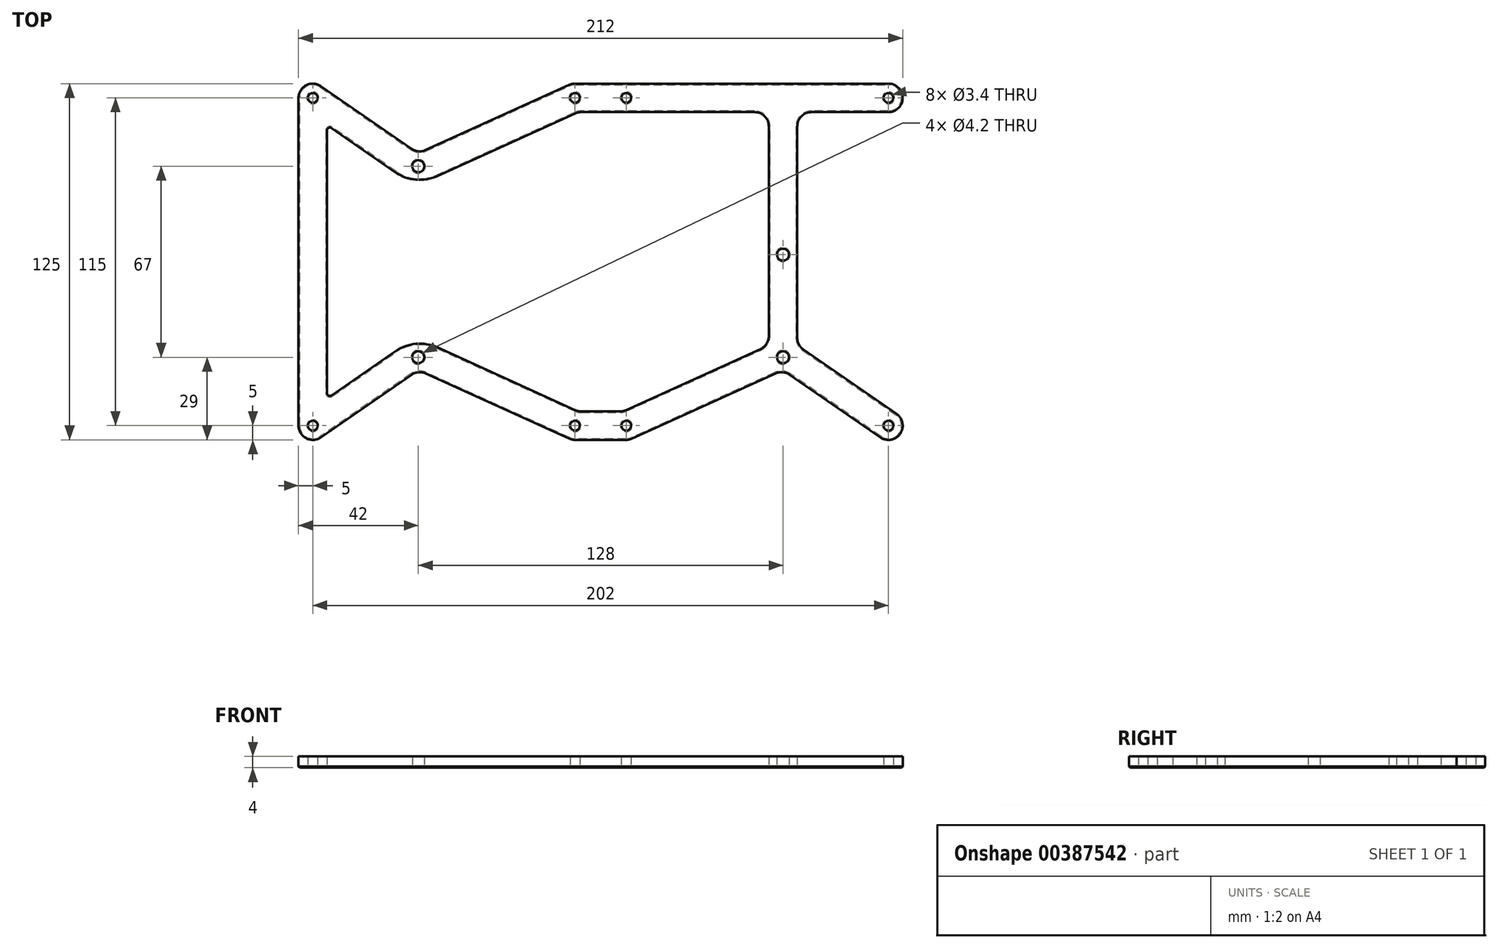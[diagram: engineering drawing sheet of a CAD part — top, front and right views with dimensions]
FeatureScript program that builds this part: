
annotation { "Feature Type Name" : "Feature", "Feature Type Description" : "" }
export const myFeature = defineFeature(function(context is Context, id is Id, definition is map)
    precondition{}
    {
        {
            var Q0;
            Q0=qCreatedBy(makeId("Top.planeOp"),FACE);
            var sketch = newSketch(context, id + "F0", { "sketchPlane" : qUnion([Q0])});
            skLineSegment(sketch, "E0", {"start": v(-64, 33.5) * mm, "end": v(-64, -33.5) * mm, "construction": true});
            skLineSegment(sketch, "E1", {"start": v(-64, -33.5) * mm, "end": v(64, -33.5) * mm, "construction": true});
            skLineSegment(sketch, "E2", {"start": v(64, -33.5) * mm, "end": v(64, 2.5) * mm, "construction": true});
            skLineSegment(sketch, "E3", {"start": v(0, 0) * mm, "end": v(0, -33.5) * mm, "construction": true});
            skCircle(sketch, "E4", {"center": v(-64, 33.5) * mm, "radius": 2.1 * mm});
            skCircle(sketch, "E5", {"center": v(-64, -33.5) * mm, "radius": 2.1 * mm});
            skCircle(sketch, "E6", {"center": v(64, -33.5) * mm, "radius": 2.1 * mm});
            skCircle(sketch, "E7", {"center": v(64, 2.5) * mm, "radius": 2.1 * mm});
            skSolve(sketch);
        }
        {
            var Q0;
            Q0=qCreatedBy(makeId("Top.planeOp"),FACE);
            var sketch = newSketch(context, id + "F1", { "sketchPlane" : qUnion([Q0])});
            skLineSegment(sketch, "E8.bottom", {"start": v(101, 57.5) * mm, "end": v(9, 57.5) * mm, "construction": true});
            skLineSegment(sketch, "E8.top", {"start": v(101, -57.5) * mm, "end": v(9, -57.5) * mm, "construction": true});
            skLineSegment(sketch, "E8.left", {"start": v(101, 57.5) * mm, "end": v(101, -57.5) * mm, "construction": true});
            skLineSegment(sketch, "E8.right", {"start": v(9, 57.5) * mm, "end": v(9, -57.5) * mm, "construction": true});
            skPoint(sketch, "E8.middle", {"position": v(55, 0) * mm});
            skCircle(sketch, "E9", {"center": v(9, 57.5) * mm, "radius": 2.1 * mm});
            skCircle(sketch, "E10", {"center": v(101, 57.5) * mm, "radius": 2.1 * mm});
            skCircle(sketch, "E11", {"center": v(101, -57.5) * mm, "radius": 2.1 * mm});
            skCircle(sketch, "E12", {"center": v(9, -57.5) * mm, "radius": 2.1 * mm});
            skLineSegment(sketch, "E13.0", {"start": v(5, 61.5) * mm, "end": v(5, -61.5) * mm, "construction": true});
            skLineSegment(sketch, "E13.1", {"start": v(105, 61.5) * mm, "end": v(5, 61.5) * mm, "construction": true});
            skLineSegment(sketch, "E13.2", {"start": v(105, 61.5) * mm, "end": v(105, -61.5) * mm, "construction": true});
            skLineSegment(sketch, "E13.3", {"start": v(105, -61.5) * mm, "end": v(5, -61.5) * mm, "construction": true});
            skLineSegment(sketch, "E14", {"start": v(0, 100) * mm, "end": v(0, -100) * mm, "construction": true});
            skCircle(sketch, "E15.MirrorC", {"center": v(-101, 57.5) * mm, "radius": 2.1 * mm});
            skCircle(sketch, "E16.MirrorC", {"center": v(-101, -57.5) * mm, "radius": 2.1 * mm});
            skCircle(sketch, "E17.MirrorC", {"center": v(-9, -57.5) * mm, "radius": 2.1 * mm});
            skCircle(sketch, "E18.MirrorC", {"center": v(-9, 57.5) * mm, "radius": 2.1 * mm});
            skLineSegment(sketch, "E19.MirrorCS", {"start": v(-5, 61.5) * mm, "end": v(-5, -61.5) * mm, "construction": true});
            skLineSegment(sketch, "E20.MirrorCS", {"start": v(-105, 61.5) * mm, "end": v(-5, 61.5) * mm, "construction": true});
            skLineSegment(sketch, "E21.MirrorCS", {"start": v(-105, 61.5) * mm, "end": v(-105, -61.5) * mm, "construction": true});
            skLineSegment(sketch, "E22.MirrorCS", {"start": v(-105, -61.5) * mm, "end": v(-5, -61.5) * mm, "construction": true});
            skPoint(sketch, "E23.MirrorP", {"position": v(-55, 0) * mm});
            skLineSegment(sketch, "E24.MirrorCS", {"start": v(-101, 57.5) * mm, "end": v(-9, 57.5) * mm, "construction": true});
            skLineSegment(sketch, "E25.MirrorCS", {"start": v(-101, -57.5) * mm, "end": v(-9, -57.5) * mm, "construction": true});
            skLineSegment(sketch, "E26.MirrorCS", {"start": v(-9, 57.5) * mm, "end": v(-9, -57.5) * mm, "construction": true});
            skLineSegment(sketch, "E27.MirrorCS", {"start": v(-101, 57.5) * mm, "end": v(-101, -57.5) * mm, "construction": true});
            skCircle(sketch, "E28", {"center": v(-101, 57.5) * mm, "radius": 1.7 * mm});
            skCircle(sketch, "E29", {"center": v(-9, 57.5) * mm, "radius": 1.7 * mm});
            skCircle(sketch, "E30", {"center": v(9, 57.5) * mm, "radius": 1.7 * mm});
            skCircle(sketch, "E31", {"center": v(101, 57.5) * mm, "radius": 1.7 * mm});
            skCircle(sketch, "E32", {"center": v(101, -57.5) * mm, "radius": 1.7 * mm});
            skCircle(sketch, "E33", {"center": v(-9, -57.5) * mm, "radius": 1.7 * mm});
            skCircle(sketch, "E34", {"center": v(9, -57.5) * mm, "radius": 1.7 * mm});
            skCircle(sketch, "E35", {"center": v(-101, -57.5) * mm, "radius": 1.7 * mm});
            skSolve(sketch);
        }
        {
            var Q0;
            Q0=qCreatedBy(makeId("Top.planeOp"),FACE);
            var sketch = newSketch(context, id + "F2", { "sketchPlane" : qUnion([Q0])});
            skLineSegment(sketch, "E36", {"start": v(-98.16, -61.61) * mm, "end": v(-66.33, -39.61) * mm});
            skLineSegment(sketch, "E37", {"start": v(-61.42, -39.17) * mm, "end": v(-11.07, -62.05) * mm});
            skLineSegment(sketch, "E38", {"start": v(-9, -62.5) * mm, "end": v(9, -62.5) * mm});
            skLineSegment(sketch, "E39", {"start": v(11.07, -62.05) * mm, "end": v(61.42, -39.17) * mm});
            skLineSegment(sketch, "E40", {"start": v(66.33, -39.61) * mm, "end": v(98.16, -61.61) * mm});
            skLineSegment(sketch, "E41", {"start": v(103.84, -53.39) * mm, "end": v(71.16, -30.8) * mm});
            skLineSegment(sketch, "E42", {"start": v(69, -26.68) * mm, "end": v(69, 47.5) * mm});
            skLineSegment(sketch, "E43", {"start": v(101, 52.5) * mm, "end": v(74, 52.5) * mm});
            skLineSegment(sketch, "E44", {"start": v(101, 62.5) * mm, "end": v(-9, 62.5) * mm});
            skLineSegment(sketch, "E45", {"start": v(-11.07, 62.05) * mm, "end": v(-61.42, 39.17) * mm});
            skLineSegment(sketch, "E46", {"start": v(-66.33, 39.61) * mm, "end": v(-98.16, 61.61) * mm});
            skLineSegment(sketch, "E47", {"start": v(-106, 57.5) * mm, "end": v(-106, -57.5) * mm});
            skArc(sketch, "E48.filletArc", {"start": v(98.16, -61.61) * mm, "mid": v(105.11, -60.34) * mm, "end": v(103.84, -53.39) * mm});
            skArc(sketch, "E49.filletArc", {"start": v(101, 52.5) * mm, "mid": v(106, 57.5) * mm, "end": v(101, 62.5) * mm});
            skPoint(sketch, "E50.visualSharp", {"position": v(69, 52.5) * mm});
            skArc(sketch, "E50.filletArc", {"start": v(74, 52.5) * mm, "mid": v(70.46, 51.04) * mm, "end": v(69, 47.5) * mm});
            skPoint(sketch, "E51.visualSharp", {"position": v(69, -29.3) * mm});
            skArc(sketch, "E51.filletArc", {"start": v(69, -26.68) * mm, "mid": v(69.57, -29) * mm, "end": v(71.16, -30.8) * mm});
            skPoint(sketch, "E52.visualSharp", {"position": v(10.08, -62.5) * mm});
            skArc(sketch, "E52.filletArc", {"start": v(9, -62.5) * mm, "mid": v(10.06, -62.39) * mm, "end": v(11.07, -62.05) * mm});
            skPoint(sketch, "E53.visualSharp", {"position": v(-10.08, -62.5) * mm});
            skArc(sketch, "E53.filletArc", {"start": v(-11.07, -62.05) * mm, "mid": v(-10.06, -62.39) * mm, "end": v(-9, -62.5) * mm});
            skPoint(sketch, "E54.visualSharp", {"position": v(-64, -38) * mm});
            skArc(sketch, "E54.filletArc", {"start": v(-61.42, -39.17) * mm, "mid": v(-63.93, -38.74) * mm, "end": v(-66.33, -39.61) * mm});
            skPoint(sketch, "E55.visualSharp", {"position": v(64, -38) * mm});
            skArc(sketch, "E55.filletArc", {"start": v(66.33, -39.61) * mm, "mid": v(63.93, -38.74) * mm, "end": v(61.42, -39.17) * mm});
            skPoint(sketch, "E56.visualSharp", {"position": v(-106, -67.04) * mm});
            skArc(sketch, "E56.filletArc", {"start": v(-106, -57.5) * mm, "mid": v(-103.32, -61.93) * mm, "end": v(-98.16, -61.61) * mm});
            skPoint(sketch, "E57.visualSharp", {"position": v(-106, 67.04) * mm});
            skArc(sketch, "E57.filletArc", {"start": v(-98.16, 61.61) * mm, "mid": v(-103.32, 61.93) * mm, "end": v(-106, 57.5) * mm});
            skPoint(sketch, "E58.visualSharp", {"position": v(-64, 38) * mm});
            skArc(sketch, "E58.filletArc", {"start": v(-66.33, 39.61) * mm, "mid": v(-63.93, 38.74) * mm, "end": v(-61.42, 39.17) * mm});
            skPoint(sketch, "E59.visualSharp", {"position": v(-10.08, 62.5) * mm});
            skArc(sketch, "E59.filletArc", {"start": v(-9, 62.5) * mm, "mid": v(-10.06, 62.39) * mm, "end": v(-11.07, 62.05) * mm});
            skLineSegment(sketch, "E60", {"start": v(-64, -38) * mm, "end": v(-64, -33.5) * mm, "construction": true});
            skLineSegment(sketch, "E61", {"start": v(64, -38) * mm, "end": v(64, -33.5) * mm, "construction": true});
            skLineSegment(sketch, "E62", {"start": v(-64, 38) * mm, "end": v(-64, 33.5) * mm, "construction": true});
            skArc(sketch, "E63.0", {"start": v(-57.28, -30.07) * mm, "mid": v(-64.82, -28.78) * mm, "end": v(-72.02, -31.39) * mm});
            skLineSegment(sketch, "E63.1", {"start": v(-94.43, -46.88) * mm, "end": v(-72.02, -31.39) * mm});
            skLineSegment(sketch, "E63.2", {"start": v(-96, 46.06) * mm, "end": v(-96, -46.06) * mm});
            skLineSegment(sketch, "E63.5", {"start": v(8.9, -52.05) * mm, "end": v(56.07, -30.62) * mm});
            skLineSegment(sketch, "E63.6", {"start": v(-6.83, -52.5) * mm, "end": v(6.83, -52.5) * mm});
            skLineSegment(sketch, "E63.7", {"start": v(59, -26.07) * mm, "end": v(59, 47.5) * mm});
            skLineSegment(sketch, "E63.9", {"start": v(54, 52.5) * mm, "end": v(-6.83, 52.5) * mm});
            skLineSegment(sketch, "E63.10", {"start": v(-57.28, -30.07) * mm, "end": v(-8.9, -52.05) * mm});
            skLineSegment(sketch, "E63.11", {"start": v(-8.9, 52.05) * mm, "end": v(-57.28, 30.07) * mm});
            skArc(sketch, "E63.12", {"start": v(-72.02, 31.39) * mm, "mid": v(-64.82, 28.78) * mm, "end": v(-57.28, 30.07) * mm});
            skLineSegment(sketch, "E63.13", {"start": v(-72.02, 31.39) * mm, "end": v(-94.43, 46.88) * mm});
            skPoint(sketch, "E64.visualSharp", {"position": v(59, 52.5) * mm});
            skArc(sketch, "E64.filletArc", {"start": v(59, 47.5) * mm, "mid": v(57.54, 51.04) * mm, "end": v(54, 52.5) * mm});
            skPoint(sketch, "E65.visualSharp", {"position": v(59, -29.29) * mm});
            skArc(sketch, "E65.filletArc", {"start": v(56.07, -30.62) * mm, "mid": v(58.2, -28.78) * mm, "end": v(59, -26.07) * mm});
            skPoint(sketch, "E66.visualSharp", {"position": v(-7.92, -52.5) * mm});
            skArc(sketch, "E66.filletArc", {"start": v(-8.9, -52.05) * mm, "mid": v(-7.9, -52.39) * mm, "end": v(-6.83, -52.5) * mm});
            skPoint(sketch, "E67.visualSharp", {"position": v(7.92, -52.5) * mm});
            skArc(sketch, "E67.filletArc", {"start": v(6.83, -52.5) * mm, "mid": v(7.9, -52.39) * mm, "end": v(8.9, -52.05) * mm});
            skPoint(sketch, "E68.visualSharp", {"position": v(-7.92, 52.5) * mm});
            skArc(sketch, "E68.filletArc", {"start": v(-6.83, 52.5) * mm, "mid": v(-7.9, 52.39) * mm, "end": v(-8.9, 52.05) * mm});
            skPoint(sketch, "E69.visualSharp", {"position": v(-96, 47.96) * mm});
            skArc(sketch, "E69.filletArc", {"start": v(-94.43, 46.88) * mm, "mid": v(-95.46, 46.94) * mm, "end": v(-96, 46.06) * mm});
            skPoint(sketch, "E70.visualSharp", {"position": v(-96, -47.96) * mm});
            skArc(sketch, "E70.filletArc", {"start": v(-96, -46.06) * mm, "mid": v(-95.46, -46.94) * mm, "end": v(-94.43, -46.88) * mm});
            skSolve(sketch);
        }
        {
            var Q0;
            Q0=qSketchRegion(id+"F2",true);
            extrude(context, id + "F3", {"entities" : qUnion([Q0]), "depth" : 4 * mm});
        }
        {
            var Q0;
            Q0=qSketchRegion(id+"F0",true);
            var Q1;
            Q1=makeQuery(id+"F1.imprint","IMPRINT",FACE,{"disambiguationData":[TD([[makeQuery(id+"F1.imprint","IMPRINT",EDGE,{"derivedFrom":sQuery(id+"F1.wireOp",EDGE,"E35")}),1.0]])]});
            var Q2;
            Q2=makeQuery(id+"F1.imprint","IMPRINT",FACE,{"disambiguationData":[TD([[makeQuery(id+"F1.imprint","IMPRINT",EDGE,{"derivedFrom":sQuery(id+"F1.wireOp",EDGE,"E28")}),1.0]])]});
            var Q3;
            Q3=makeQuery(id+"F1.imprint","IMPRINT",FACE,{"disambiguationData":[TD([[makeQuery(id+"F1.imprint","IMPRINT",EDGE,{"derivedFrom":sQuery(id+"F1.wireOp",EDGE,"E29")}),1.0]])]});
            var Q4;
            Q4=makeQuery(id+"F1.imprint","IMPRINT",FACE,{"disambiguationData":[TD([[makeQuery(id+"F1.imprint","IMPRINT",EDGE,{"derivedFrom":sQuery(id+"F1.wireOp",EDGE,"E30")}),1.0]])]});
            var Q5;
            Q5=makeQuery(id+"F1.imprint","IMPRINT",FACE,{"disambiguationData":[TD([[makeQuery(id+"F1.imprint","IMPRINT",EDGE,{"derivedFrom":sQuery(id+"F1.wireOp",EDGE,"E33")}),1.0]])]});
            var Q6;
            Q6=makeQuery(id+"F1.imprint","IMPRINT",FACE,{"disambiguationData":[TD([[makeQuery(id+"F1.imprint","IMPRINT",EDGE,{"derivedFrom":sQuery(id+"F1.wireOp",EDGE,"E34")}),1.0]])]});
            var Q7;
            Q7=makeQuery(id+"F1.imprint","IMPRINT",FACE,{"disambiguationData":[TD([[makeQuery(id+"F1.imprint","IMPRINT",EDGE,{"derivedFrom":sQuery(id+"F1.wireOp",EDGE,"E32")}),1.0]])]});
            var Q8;
            Q8=makeQuery(id+"F1.imprint","IMPRINT",FACE,{"disambiguationData":[TD([[makeQuery(id+"F1.imprint","IMPRINT",EDGE,{"derivedFrom":sQuery(id+"F1.wireOp",EDGE,"E31")}),1.0]])]});
            extrude(context, id + "F4", {"entities" : qUnion([Q0, Q1, Q2, Q3, Q4, Q5, Q6, Q7, Q8]), "operationType" : NewBodyOperationType.REMOVE, "endBound" : BoundingType.THROUGH_ALL, "depth" : 25 * mm});
        }
        {
            var Q0;
            Q0=makeQuery(id+"F3.opExtrude","CAP_FACE",FACE,{"disambiguationData":[OSD([sQuery(id+"F2.wireOp",EDGE,"E36"),sQuery(id+"F2.wireOp",EDGE,"E37"),sQuery(id+"F2.wireOp",EDGE,"E38"),sQuery(id+"F2.wireOp",EDGE,"E39"),sQuery(id+"F2.wireOp",EDGE,"E40"),sQuery(id+"F2.wireOp",EDGE,"E41"),sQuery(id+"F2.wireOp",EDGE,"E42"),sQuery(id+"F2.wireOp",EDGE,"E43"),sQuery(id+"F2.wireOp",EDGE,"E44"),sQuery(id+"F2.wireOp",EDGE,"E45"),sQuery(id+"F2.wireOp",EDGE,"E46"),sQuery(id+"F2.wireOp",EDGE,"E47"),sQuery(id+"F2.wireOp",EDGE,"E48.filletArc"),sQuery(id+"F2.wireOp",EDGE,"E49.filletArc"),sQuery(id+"F2.wireOp",EDGE,"E50.filletArc"),sQuery(id+"F2.wireOp",EDGE,"E51.filletArc"),sQuery(id+"F2.wireOp",EDGE,"E52.filletArc"),sQuery(id+"F2.wireOp",EDGE,"E53.filletArc"),sQuery(id+"F2.wireOp",EDGE,"E54.filletArc"),sQuery(id+"F2.wireOp",EDGE,"E55.filletArc"),sQuery(id+"F2.wireOp",EDGE,"E56.filletArc"),sQuery(id+"F2.wireOp",EDGE,"E57.filletArc"),sQuery(id+"F2.wireOp",EDGE,"E58.filletArc"),sQuery(id+"F2.wireOp",EDGE,"E59.filletArc"),sQuery(id+"F2.wireOp",EDGE,"E63.0"),sQuery(id+"F2.wireOp",EDGE,"E63.1"),sQuery(id+"F2.wireOp",EDGE,"E63.2"),sQuery(id+"F2.wireOp",EDGE,"E63.5"),sQuery(id+"F2.wireOp",EDGE,"E63.6"),sQuery(id+"F2.wireOp",EDGE,"E63.7"),sQuery(id+"F2.wireOp",EDGE,"E63.9"),sQuery(id+"F2.wireOp",EDGE,"E63.10"),sQuery(id+"F2.wireOp",EDGE,"E63.11"),sQuery(id+"F2.wireOp",EDGE,"E63.12"),sQuery(id+"F2.wireOp",EDGE,"E63.13"),sQuery(id+"F2.wireOp",EDGE,"E64.filletArc"),sQuery(id+"F2.wireOp",EDGE,"E65.filletArc"),sQuery(id+"F2.wireOp",EDGE,"E66.filletArc"),sQuery(id+"F2.wireOp",EDGE,"E67.filletArc"),sQuery(id+"F2.wireOp",EDGE,"E68.filletArc"),sQuery(id+"F2.wireOp",EDGE,"E69.filletArc"),sQuery(id+"F2.wireOp",EDGE,"E70.filletArc")])],"isStart":true});
            chamfer(context, id + "F5", {"entities" : qUnion([Q0]), "width" : 0.4 * mm, "tangentPropagation" : true});
        }
    });
